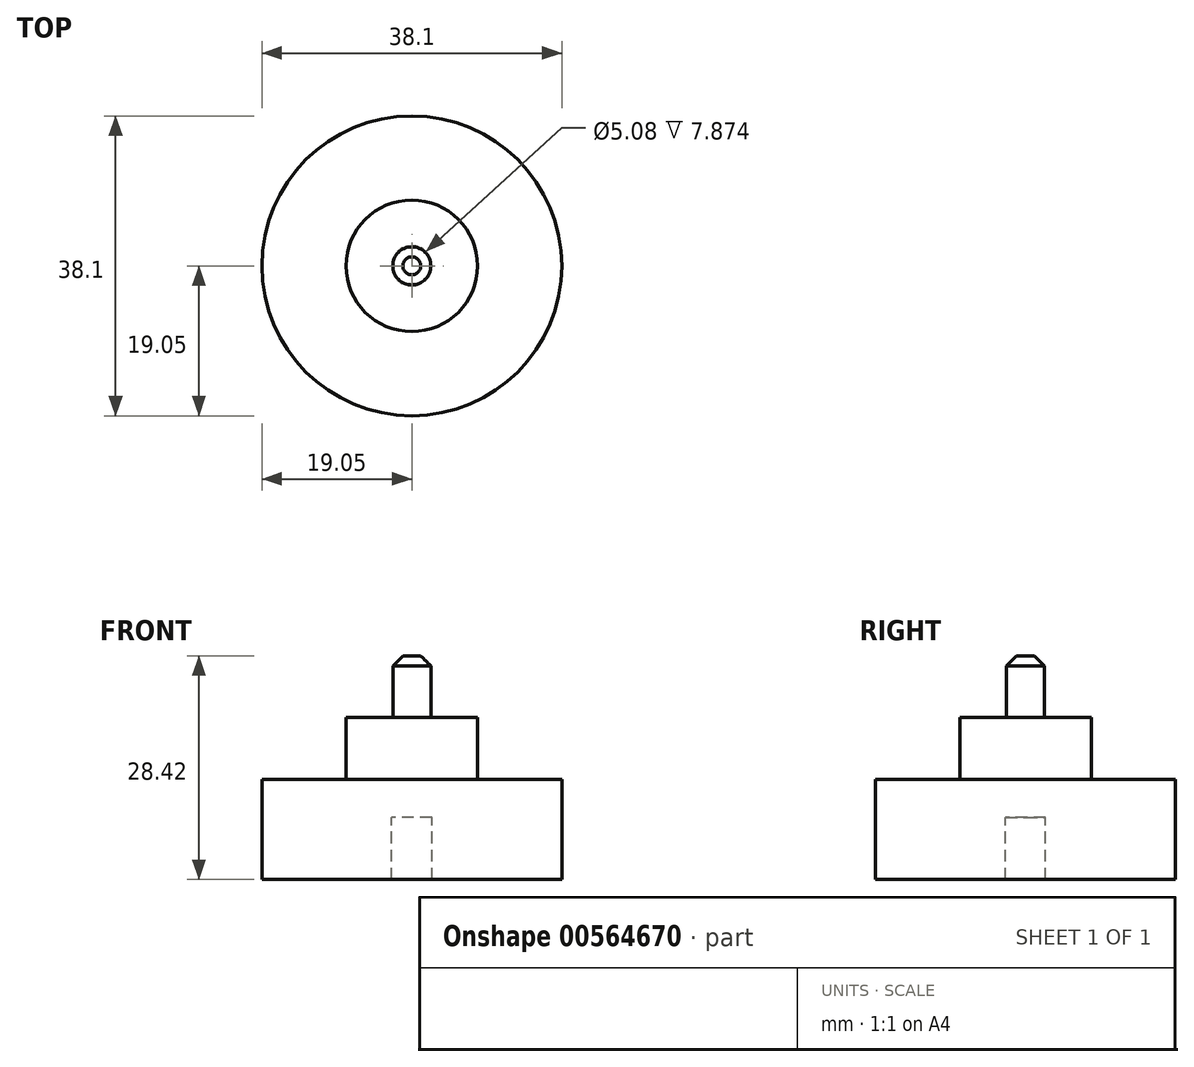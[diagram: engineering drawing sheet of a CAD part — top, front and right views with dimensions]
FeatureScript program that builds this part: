
annotation { "Feature Type Name" : "Feature", "Feature Type Description" : "" }
export const myFeature = defineFeature(function(context is Context, id is Id, definition is map)
    precondition{}
    {
        {
            var Q0;
            Q0=qCreatedBy(makeId("Front.planeOp"),FACE);
            var sketch = newSketch(context, id + "F0", { "sketchPlane" : qUnion([Q0])});
            skLineSegment(sketch, "E0", {"start": v(19.05, 0) * mm, "end": v(19.05, 12.7) * mm});
            skLineSegment(sketch, "E1", {"start": v(19.05, 12.7) * mm, "end": v(8.36, 12.7) * mm});
            skLineSegment(sketch, "E2", {"start": v(2.41, 20.57) * mm, "end": v(8.36, 20.57) * mm});
            skLineSegment(sketch, "E3", {"start": v(8.36, 20.57) * mm, "end": v(8.36, 12.7) * mm});
            skLineSegment(sketch, "E4", {"start": v(0, 0) * mm, "end": v(2.54, 0) * mm});
            skLineSegment(sketch, "E5", {"start": v(2.54, 0) * mm, "end": v(2.54, 7.87) * mm});
            skLineSegment(sketch, "E6", {"start": v(2.54, 7.87) * mm, "end": v(0, 7.87) * mm});
            skLineSegment(sketch, "E7", {"start": v(2.54, 0) * mm, "end": v(19.05, 0) * mm});
            skLineSegment(sketch, "E8", {"start": v(0, 28.42) * mm, "end": v(2.41, 28.42) * mm});
            skLineSegment(sketch, "E9", {"start": v(2.41, 28.42) * mm, "end": v(2.41, 20.57) * mm});
            skPoint(sketch, "E10.start.orphan", {"position": v(0, 20.57) * mm});
            skLineSegment(sketch, "E11", {"start": v(0, 28.42) * mm, "end": v(0, 7.87) * mm});
            skSolve(sketch);
        }
        {
            var Q0;
            Q0 = qSketchRegion(id + "F0", true);
            var Q1;
            Q1=sQuery(id+"F0.wireOp",EDGE,"E11");
            revolve(context, id + "F1", {"entities" : qUnion([Q0]), "axis" : qUnion([Q1]), "revolveType" : RevolveType.FULL});
        }
        {
            var Q0;
            Q0=makeQuery(id+"F1.opRevolve","SWEPT_EDGE",EDGE,{"disambiguationData":[OSD([sQuery(id+"F0.wireOp",EDGE,"E8"),sQuery(id+"F0.wireOp",EDGE,"E9")])]});
            chamfer(context, id + "F2", {"entities" : qUnion([Q0]), "width" : 1.27 * mm, "tangentPropagation" : true});
        }
    });
